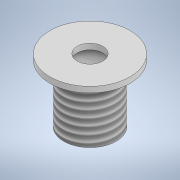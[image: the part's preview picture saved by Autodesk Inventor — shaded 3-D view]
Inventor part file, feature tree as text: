
AUTODESK INVENTOR PART (.ipt)
format: ipt  version: 2022.2 (Build 262287000, 287)  size: 123,904 bytes
history: native  units: mm
features: extrude x3, sketch x3, thread x1
ambient origin geometry x8: Origin, YZ Plane, XZ Plane, XY Plane, X Axis, Y Axis, Z Axis, Center Point
bodies: Body1 (feature_tree)
feature tree (7):
  extrude  "Extrusion2"  Depth=1.7mm
  extrude  "Extrusion3"  Depth=2.0mm
  thread  "Thread1"  [1 undecoded]
  extrude  "Extrusion4"  Depth=2.0mm
  sketch  "Sketch1"  dims[d0=18.3mm d4=1.7mm]
  sketch  "Sketch2"  dims[d5=20.0mm d6=0.0mm d7=28.0mm d8=2.0mm d9=0.0mm]
  sketch  "Sketch3"  dims[d10=20.0mm d11=0.0mm d12=9.0mm d13=9.0mm d14=2.0mm d15=0.0mm]
note: 1 required parameter value undecoded (feature->parameter linkage not recoverable at this tier; creation-order binding heuristic only, values carry confidence <= 0.55)
